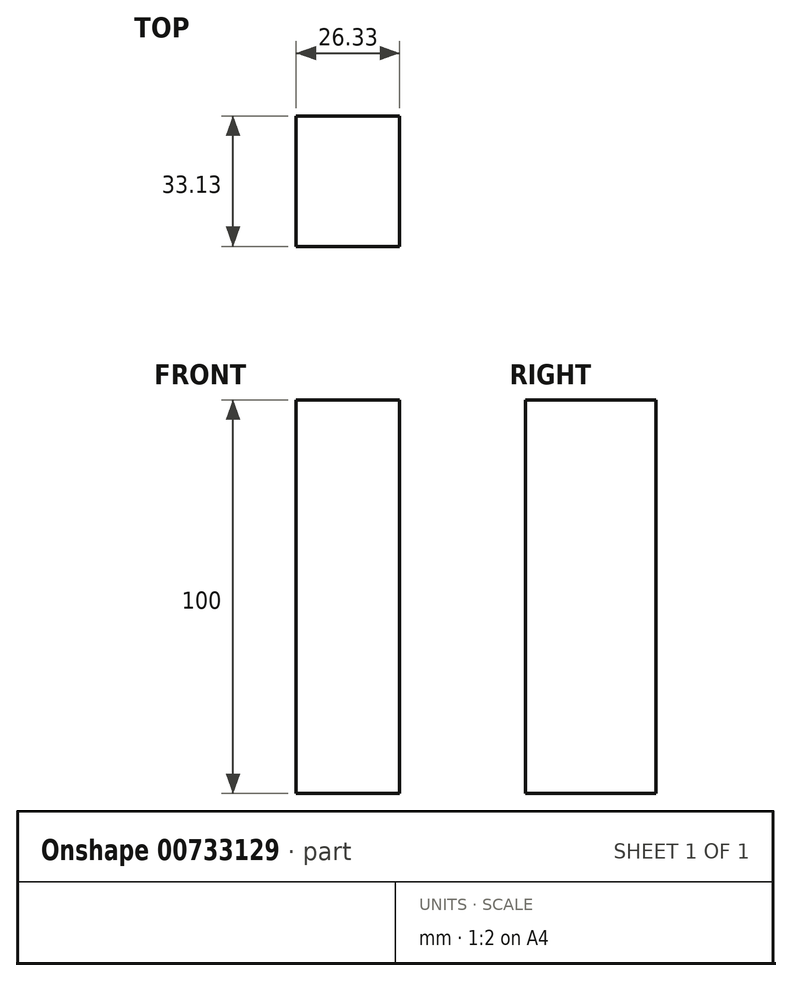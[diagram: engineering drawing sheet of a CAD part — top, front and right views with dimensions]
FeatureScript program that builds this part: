
annotation { "Feature Type Name" : "Feature", "Feature Type Description" : "" }
export const myFeature = defineFeature(function(context is Context, id is Id, definition is map)
    precondition{}
    {
        {
            var Q0;
            Q0=qCreatedBy(makeId("Top.planeOp"),FACE);
            var sketch = newSketch(context, id + "F0", { "sketchPlane" : qUnion([Q0])});
            skLineSegment(sketch, "E0.bottom", {"start": v(-61.32, -44.05) * mm, "end": v(-35, -44.05) * mm});
            skLineSegment(sketch, "E0.top", {"start": v(-61.32, -10.92) * mm, "end": v(-35, -10.92) * mm});
            skLineSegment(sketch, "E0.left", {"start": v(-61.32, -44.05) * mm, "end": v(-61.32, -10.92) * mm});
            skLineSegment(sketch, "E0.right", {"start": v(-35, -44.05) * mm, "end": v(-35, -10.92) * mm});
            skSolve(sketch);
        }
        {
            var Q0;
            Q0 = qSketchRegion(id + "F0", true);
            extrude(context, id + "F1", {"entities" : qUnion([Q0]), "depth" : 100 * mm, "offsetDistance" : 25 * mm});
        }
    });
